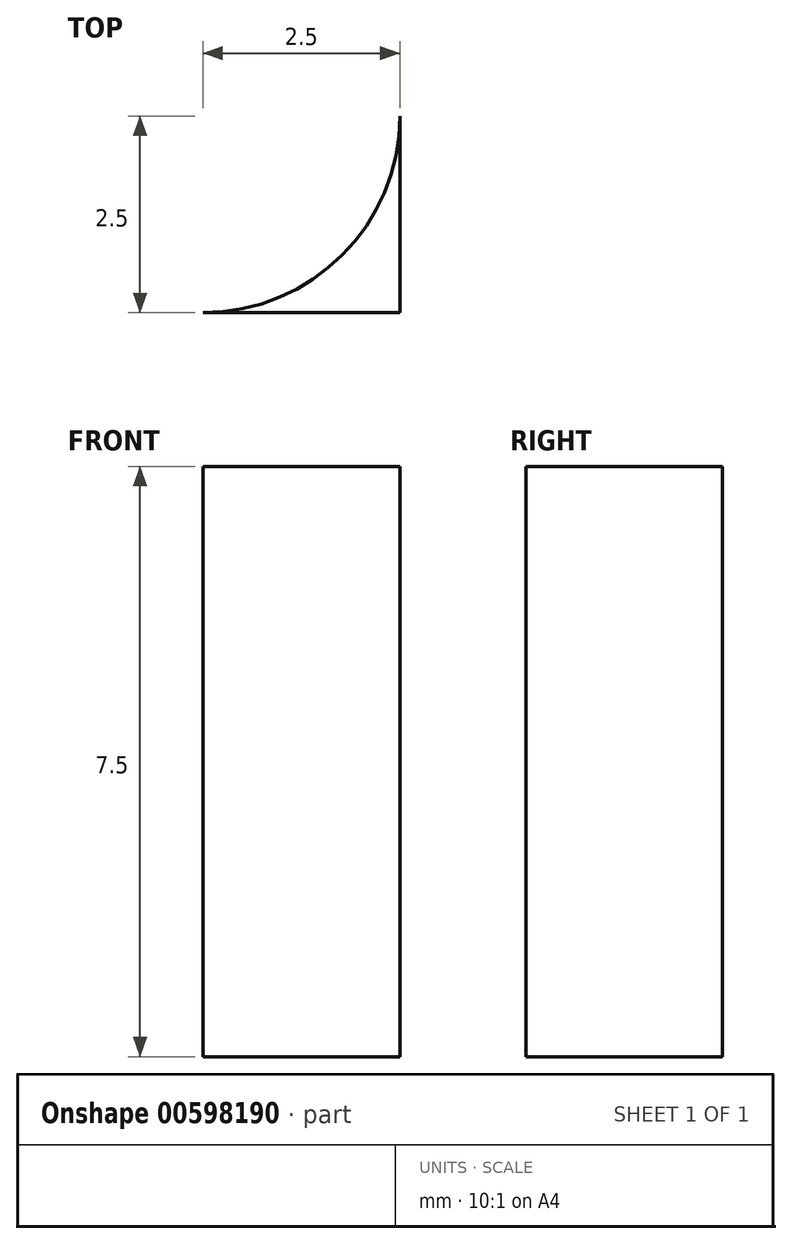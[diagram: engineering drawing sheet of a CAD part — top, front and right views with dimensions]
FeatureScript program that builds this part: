
annotation { "Feature Type Name" : "Feature", "Feature Type Description" : "" }
export const myFeature = defineFeature(function(context is Context, id is Id, definition is map)
    precondition{}
    {
        {
            var Q0;
            Q0=qCreatedBy(makeId("Front.planeOp"),FACE);
            var sketch = newSketch(context, id + "F0", { "sketchPlane" : qUnion([Q0])});
            skLineSegment(sketch, "E0", {"start": v(-45, 0) * mm, "end": v(45, 0) * mm});
            skLineSegment(sketch, "E1", {"start": v(-45, 65) * mm, "end": v(45, 65) * mm});
            skLineSegment(sketch, "E2", {"start": v(45, 65) * mm, "end": v(45, 0) * mm});
            skLineSegment(sketch, "E3", {"start": v(-45, 65) * mm, "end": v(-45, 0) * mm});
            skSolve(sketch);
        }
        {
            var Q0;
            Q0 = qSketchRegion(id + "F0", true);
            extrude(context, id + "F1", {"entities" : qUnion([Q0]), "depth" : 30 * mm, "offsetDistance" : 25 * mm});
        }
        {
            var Q0;
            Q0=makeQuery(id+"F1.opExtrude","SWEPT_FACE",FACE,{"disambiguationData":[OSD([sQuery(id+"F0.wireOp",EDGE,"E2")])]});
            var sketch = newSketch(context, id + "F2", { "sketchPlane" : qUnion([Q0])});
            skLineSegment(sketch, "E4", {"start": v(-123.24, 7.5) * mm, "end": v(-5, 7.5) * mm});
            skLineSegment(sketch, "E5", {"start": v(-5, 7.5) * mm, "end": v(-5, 109.88) * mm});
            skLineSegment(sketch, "E6", {"start": v(-123.24, 7.5) * mm, "end": v(-5, 109.88) * mm});
            skSolve(sketch);
        }
        {
            var Q0;
            Q0 = qSketchRegion(id + "F2", true);
            extrude(context, id + "F3", {"entities" : qUnion([Q0]), "operationType" : NewBodyOperationType.REMOVE, "endBound" : BoundingType.THROUGH_ALL, "oppositeDirection" : true, "depth" : 25 * mm, "offsetDistance" : 25 * mm});
        }
        {
            var Q0;
            Q0=makeQuery(id+"F3.boolean.opBoolean","COPY",FACE,{"derivedFrom":makeQuery(id+"F3.opExtrude","SWEPT_FACE",FACE,{"disambiguationData":[OSD([sQuery(id+"F2.wireOp",EDGE,"E5")])]})});
            var sketch = newSketch(context, id + "F4", { "sketchPlane" : qUnion([Q0])});
            skArc(sketch, "E7", {"start": v(2.5, 32.75) * mm, "mid": v(0, 57.5) * mm, "end": v(-2.5, 32.75) * mm});
            skCircle(sketch, "E8", {"center": v(0, 45) * mm, "radius": 7.5 * mm});
            skLineSegment(sketch, "E9", {"start": v(-45, 12.5) * mm, "end": v(-9.41, 53.23) * mm});
            skLineSegment(sketch, "E10.MirrorCS", {"start": v(45, 12.5) * mm, "end": v(9.41, 53.23) * mm});
            skLineSegment(sketch, "E11", {"start": v(-2.5, 7.5) * mm, "end": v(-2.5, 32.75) * mm});
            skLineSegment(sketch, "E12", {"start": v(2.5, 7.5) * mm, "end": v(2.5, 32.75) * mm});
            skPoint(sketch, "E13", {"position": v(-2.5, 7.5) * mm});
            skPoint(sketch, "E14", {"position": v(2.5, 7.5) * mm});
            skSolve(sketch);
        }
        {
            var Q0;
            {var subQ4=sQuery(id+"F4.wireOp",EDGE,"E9");Q0=makeQuery(id+"F4.imprint","IMPRINT",FACE,{"disambiguationData":[TD([[makeQuery(id+"F4.imprint","IMPRINT",EDGE,{"derivedFrom":subQ4}),1.0]])]});}
            extrude(context, id + "F5", {"entities" : qUnion([Q0]), "operationType" : NewBodyOperationType.REMOVE, "endBound" : BoundingType.THROUGH_ALL, "oppositeDirection" : true, "depth" : 25 * mm, "offsetDistance" : 25 * mm});
        }
        {
            var Q0;
            Q0=makeQuery(id+"F4.imprint","IMPRINT",FACE,{"disambiguationData":[TD([[makeQuery(id+"F4.imprint","IMPRINT",EDGE,{"derivedFrom":sQuery(id+"F4.wireOp",EDGE,"E8")}),-1.0]])]});
            extrude(context, id + "F6", {"entities" : qUnion([Q0]), "operationType" : NewBodyOperationType.ADD, "depth" : 25 * mm, "offsetDistance" : 25 * mm});
        }
        {
            var Q0;
            {var subQ1=sQuery(id+"F0.wireOp",EDGE,"E3");var subQ3=sQuery(id+"F2.wireOp",EDGE,"E4");Q0=makeQuery(id+"F6.boolean.opBoolean","SPLIT",FACE,{"disambiguationData":[TD([makeQuery(id+"F1.opExtrude","SWEPT_FACE",FACE,{"disambiguationData":[OSD([subQ1])]})])],"derivedFrom":makeQuery(id+"F3.boolean.opBoolean","COPY",FACE,{"derivedFrom":makeQuery(id+"F3.opExtrude","SWEPT_FACE",FACE,{"disambiguationData":[OSD([subQ3])]})})});}
            var sketch = newSketch(context, id + "F7", { "sketchPlane" : qUnion([Q0])});
            skCircle(sketch, "E15", {"center": v(-35, -20) * mm, "radius": 1.88 * mm});
            skCircle(sketch, "E16", {"center": v(-15, -15) * mm, "radius": 1.88 * mm});
            skCircle(sketch, "E17.MirrorC", {"center": v(15, -15) * mm, "radius": 1.88 * mm});
            skCircle(sketch, "E18.MirrorC", {"center": v(35, -20) * mm, "radius": 1.88 * mm});
            skSolve(sketch);
        }
        {
            var Q0;
            Q0=makeQuery(id+"F7.imprint","IMPRINT",FACE,{"disambiguationData":[TD([[makeQuery(id+"F7.imprint","IMPRINT",EDGE,{"derivedFrom":sQuery(id+"F7.wireOp",EDGE,"E15")}),1.0]])]});
            var Q1;
            Q1=makeQuery(id+"F7.imprint","IMPRINT",FACE,{"disambiguationData":[TD([[makeQuery(id+"F7.imprint","IMPRINT",EDGE,{"derivedFrom":sQuery(id+"F7.wireOp",EDGE,"E16")}),1.0]])]});
            var Q2;
            Q2=makeQuery(id+"F7.imprint","IMPRINT",FACE,{"disambiguationData":[TD([[makeQuery(id+"F7.imprint","IMPRINT",EDGE,{"derivedFrom":sQuery(id+"F7.wireOp",EDGE,"E17.MirrorC")}),-1.0]])]});
            var Q3;
            Q3=makeQuery(id+"F7.imprint","IMPRINT",FACE,{"disambiguationData":[TD([[makeQuery(id+"F7.imprint","IMPRINT",EDGE,{"derivedFrom":sQuery(id+"F7.wireOp",EDGE,"E18.MirrorC")}),-1.0]])]});
            extrude(context, id + "F8", {"entities" : qUnion([Q0, Q1, Q2, Q3]), "operationType" : NewBodyOperationType.REMOVE, "endBound" : BoundingType.THROUGH_ALL, "oppositeDirection" : true, "depth" : 25 * mm, "offsetDistance" : 25 * mm});
        }
        {
            var Q0;
            Q0=makeQuery(id+"F1.opExtrude","SWEPT_FACE",FACE,{"disambiguationData":[OSD([sQuery(id+"F0.wireOp",EDGE,"E0")])]});
            var sketch = newSketch(context, id + "F9", { "sketchPlane" : qUnion([Q0])});
            skArc(sketch, "E19", {"start": v(-42.5, 30) * mm, "mid": v(-44.27, 29.27) * mm, "end": v(-45, 27.5) * mm});
            skPoint(sketch, "E20", {"position": v(-42.5, 30) * mm});
            skPoint(sketch, "E21", {"position": v(-45, 27.5) * mm});
            skArc(sketch, "E22.MirrorCS", {"start": v(42.5, 30) * mm, "mid": v(44.27, 29.27) * mm, "end": v(45, 27.5) * mm});
            skSolve(sketch);
        }
        {
            var Q0;
            {var subQ0=sQuery(id+"F9.wireOp",EDGE,"E22.MirrorCS");Q0=makeQuery(id+"F9.imprint","IMPRINT",FACE,{"disambiguationData":[TD([[makeQuery(id+"F9.imprint","IMPRINT",EDGE,{"derivedFrom":subQ0}),1.0]])]});}
            var Q1;
            {var subQ0=sQuery(id+"F9.wireOp",EDGE,"E19");Q1=makeQuery(id+"F9.imprint","IMPRINT",FACE,{"disambiguationData":[TD([[makeQuery(id+"F9.imprint","IMPRINT",EDGE,{"derivedFrom":subQ0}),-1.0]])]});}
            extrude(context, id + "F10", {"entities" : qUnion([Q0, Q1]), "operationType" : NewBodyOperationType.REMOVE, "endBound" : BoundingType.THROUGH_ALL, "oppositeDirection" : true, "depth" : 25 * mm, "offsetDistance" : 25 * mm});
        }
    });
